# Revit family: Montageschiene 45- 90-2,0 D  6m fbv
name_source: partatom
category: HLS-Bauteile
revit_build: Autodesk Revit 2017 (Build: 20190507_1515(x64)
units: mm (PartAtom-declared; Revit-internal decimal feet)

## family parameters
Arbeitsebenenbasiert = Ja
Beim Laden mit Abzugskörper schneiden = Nein
Bemaßung runder Anschluss = Durchmesser verwenden
Gemeinsam genutzt = Ja
Immer vertikal = Nein
Raumberechnungspunkt = Nein
Teiletyp = Normal

## types (1)
- C-Profil 45- 90-2,0 D  L=6000 fbv
    Abmessung = 45/90/2.0 mm
    Artikelnummer = 0821901620
    Breite = 45 mm  [stored 0.147638 ft]
    Bund = 180 m
    EAN = 4250928448125
    Fabrikat = MEFA
    Firma = MEFA Befestigungs- und Montagesysteme GmbH
    Fläche (schwächster Profilquerschnitt) = 0 m²
    Gewicht = 4,90 kg
    Höhe = 90 mm
    Kurztext1 = Montageschiene C-Profil doppelt
    Kurztext2 = 45 / 90 / 2 mm L= 6 m fbv
    Langloch = 14.0 x 45.0 mm
    Lochdurchmesser = 14.00 mm
    Länge = 6000 mm  [stored 19.685 ft]
    Material = Stahl
    Materialname = S250
    Mengeneinheit = m
    Oberflaeche = feuerbandverzinkt
    Schlitzbreite = 22 mm
    Schwerpunktabstand eo = 4,5 cm
    Schwerpunktabstand eu = 4,5 cm
    Schwerpunktabstand ez = 2,25 cm
    Streckgrenze = 250 N/mm²
    Stärke = 2 mm  [stored 0.00656168 ft]
    Torsionswiderstandsmoment Wt = cm³
    Trägheitsradius iy = 2,78 cm
    Trägheitsradius iz = 1,89 cm
    Vorgabe-Ansicht = 1219 mm
    Widerstandsmoment Wy = 10,25 cm³
    Widerstandsmoment Wz = 9,47 cm³
    vpe = 24 m

note: [stored X ft] marks values corroborated as IEEE doubles in the binary element streams (Revit-internal decimal feet)
